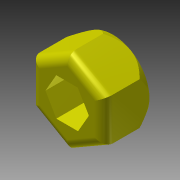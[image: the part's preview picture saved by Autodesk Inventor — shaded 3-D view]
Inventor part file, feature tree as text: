
AUTODESK INVENTOR PART (.ipt)
format: ipt  version: 2013 (Build 170138000, 138)  size: 143,872 bytes
history: native  units: in
note: dims shown in document units (in); Inventor stores cm internally (conversion verified against a paired STEP export)
features: extrude x4, sketch x4, fillet x1
ambient origin geometry x8: Origin, YZ Plane, XZ Plane, XY Plane, X Axis, Y Axis, Z Axis, Center Point
bodies: Solid1 (feature_tree)
feature tree (9):
  extrude  "Extrusion1"  Depth=0.25in TaperAngle=0.0deg
  extrude  "Extrusion2"  Depth=0.375in TaperAngle=0.0deg
  extrude  "Extrusion4"  Depth=0.3438in
  extrude  "Extrusion5"  Depth=0.125in
  fillet  "Fillet2"  [1 undecoded]
  sketch  "Sketch1"  dims[d0=1.0in d1=0.25in d2=0.0in]
  sketch  "Sketch2"  dims[d3=0.515in d4=0.375in d5=0.0in]
  sketch  "Sketch4"  dims[d10=0.25in d11=30.0deg d13=0.3438in]
  sketch  "Sketch5"  dims[d15=0.25in d16=0.0in d18=0.125in]
note: 1 required parameter value undecoded (feature->parameter linkage not recoverable at this tier; creation-order binding heuristic only, values carry confidence <= 0.55)
